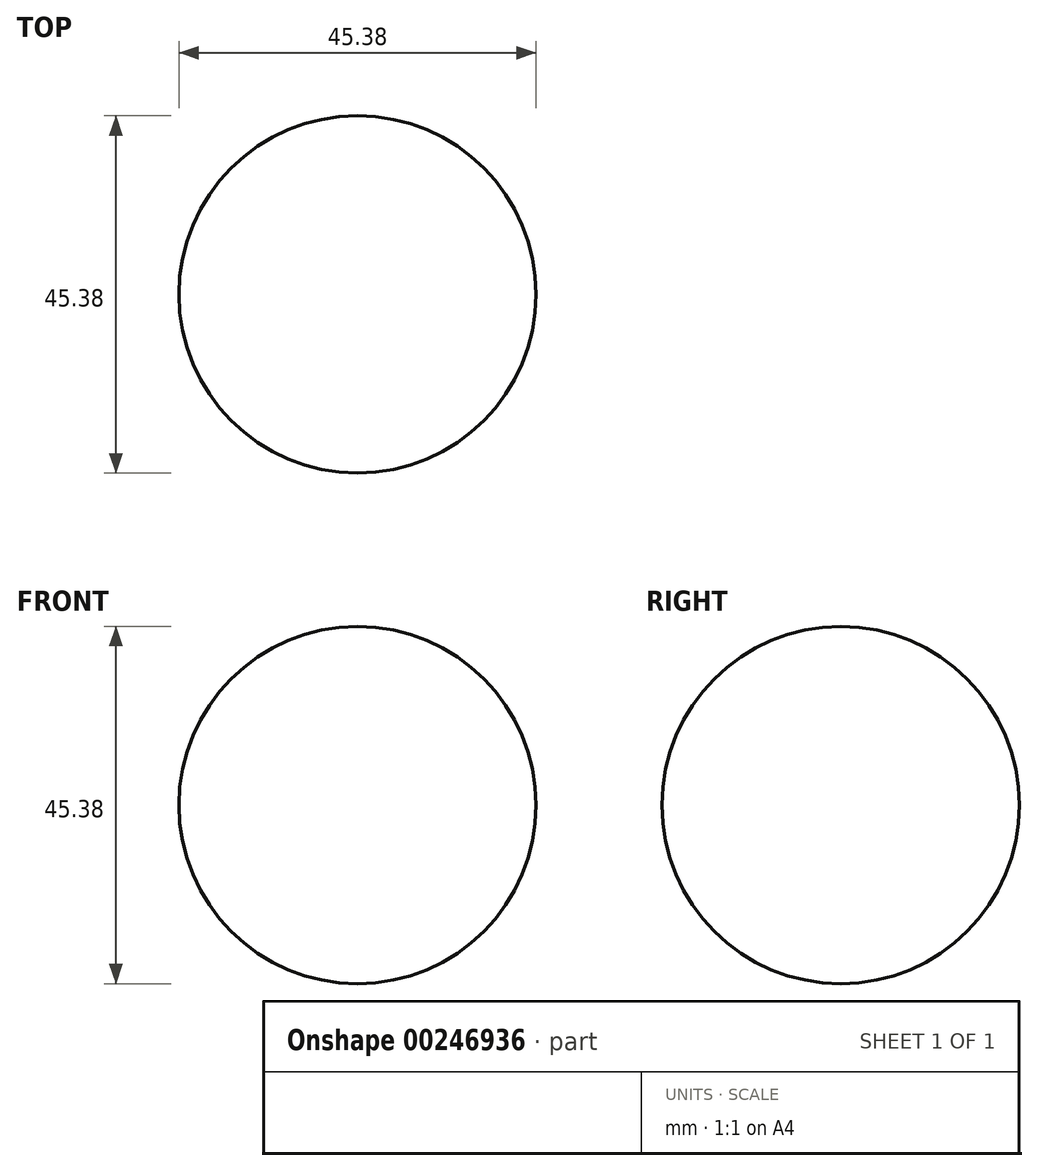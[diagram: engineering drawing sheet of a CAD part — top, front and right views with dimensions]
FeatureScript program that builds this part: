
annotation { "Feature Type Name" : "Feature", "Feature Type Description" : "" }
export const myFeature = defineFeature(function(context is Context, id is Id, definition is map)
    precondition{}
    {
        {
            var Q0;
            Q0=qCreatedBy(makeId("Front.planeOp"),FACE);
            var sketch = newSketch(context, id + "F0", { "sketchPlane" : qUnion([Q0])});
            skLineSegment(sketch, "E0", {"start": v(0, 0) * mm, "end": v(0, 45.38) * mm});
            skArc(sketch, "E1", {"start": v(0, 45.38) * mm, "mid": v(22.69, 22.69) * mm, "end": v(0, 0) * mm});
            skSolve(sketch);
        }
        {
            var Q0;
            Q0 = qSketchRegion(id + "F0", true);
            var Q1;
            Q1=sQuery(id+"F0.wireOp",EDGE,"E0");
            revolve(context, id + "F1", {"entities" : qUnion([Q0]), "axis" : qUnion([Q1]), "revolveType" : RevolveType.FULL});
        }
    });
